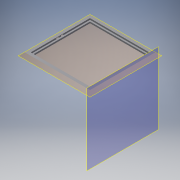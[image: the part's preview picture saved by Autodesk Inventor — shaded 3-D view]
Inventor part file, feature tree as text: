
AUTODESK INVENTOR PART (.ipt)
format: ipt  version: 2018 (Build 220112000, 112)  size: 174,080 bytes
history: native  units: mm
features: reference x19, other x10, extrude x4, sketch x4, plane x2, chamfer x1
ambient origin geometry x8: Origin, YZ Plane, XZ Plane, XY Plane, X Axis, Y Axis, Z Axis, Center Point
bodies: Volumenkörper1 (feature_tree)
feature tree (40):
  extrude  "Extrusion1"  Depth=20.0mm TaperAngle=45.0deg
  chamfer  "Fase1"  Distance=17.0mm
  plane  "Arbeitsebene1"
  extrude  "Extrusion2"  Depth=10.0mm
  extrude  "Extrusion3"  Depth=10.0mm
  plane  "Arbeitsebene3"
  extrude  "Extrusion4"  Depth=10.0mm TaperAngle=0.0deg
  sketch  "Skizze1"  dims[d0=20.0mm d1=0.0mm d2=20.0mm d3=2.0mm d4=45.0deg]
  reference  "Referenz1"
  reference  "Referenz2"
  reference  "Referenz3"
  reference  "Referenz4"
  reference  "Referenz5"
  sketch  "Skizze3"  dims[d5=-20.0mm d6=17.0mm d7=0.0mm]
  reference  "Referenz12"
  reference  "Referenz13"
  reference  "Referenz14"
  reference  "Referenz15"
  reference  "Referenz16"
  reference  "Referenz17"
  reference  "Referenz18"
  reference  "Referenz19"
  sketch  "Skizze5"  dims[d8=10.0mm d9=10.0mm]
  sketch  "Skizze6"  dims[d10=10.0mm d11=10.0mm d12=10.0mm d13=0.0mm d14=25.0mm d15=0.0mm]
  reference  "Referenz20"
  reference  "Referenz21"
  reference  "Referenz22"
  reference  "Referenz23"
  reference  "Referenz24"
  reference  "Referenz25"
  parser-record x1  (decoder bookkeeping rows leaked as tree rows — omitted from the tree; the rows remain in map.json)
  other  "SmartCube_Quadratisch.iam"
  other  "Wand2_MIR:1"
  other  "Wand1:1"
  other  "Wand1_MIR:1"
  other  "Wand2:1"
  other  "PV_Modul:1"
  other  "<userpath>\Documents\Dipl\Smartcube_Construction\Version_3\Baugruppe1.iam"
  other  "Baugruppe1.iam"
  other  "PV_Ramen_CPY_3_2:1"
note: 1 file-system path scrubbed to <path> (originals preserved in map.json)
